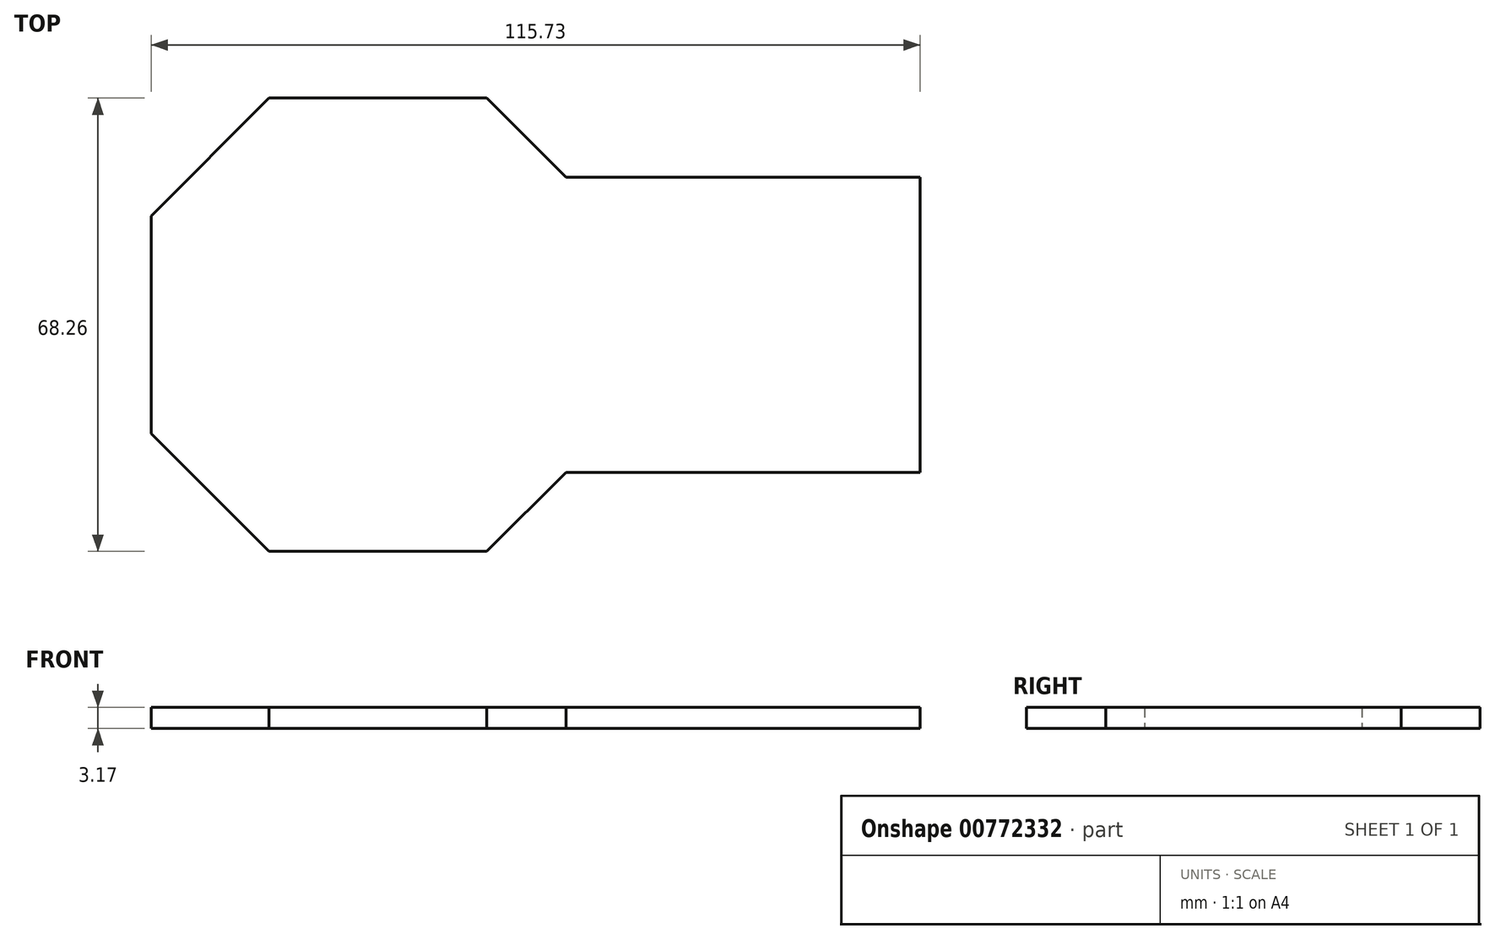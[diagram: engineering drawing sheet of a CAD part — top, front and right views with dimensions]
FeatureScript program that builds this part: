
annotation { "Feature Type Name" : "Feature", "Feature Type Description" : "" }
export const myFeature = defineFeature(function(context is Context, id is Id, definition is map)
    precondition{}
    {
        {
            var Q0;
            Q0=qCreatedBy(makeId("Top.planeOp"),FACE);
            var sketch = newSketch(context, id + "F0", { "sketchPlane" : qUnion([Q0])});
            skLineSegment(sketch, "E0.bottom", {"start": v(0, 0) * mm, "end": v(115.73, 0) * mm});
            skLineSegment(sketch, "E0.top", {"start": v(0, 68.26) * mm, "end": v(115.73, 68.26) * mm});
            skLineSegment(sketch, "E0.left", {"start": v(0, 0) * mm, "end": v(0, 68.26) * mm});
            skLineSegment(sketch, "E0.right", {"start": v(115.73, 0) * mm, "end": v(115.73, 68.26) * mm});
            skPoint(sketch, "E1", {"position": v(115.73, 11.9) * mm});
            skPoint(sketch, "E2", {"position": v(115.73, 56.36) * mm});
            skPoint(sketch, "E3", {"position": v(3.18, 3.18) * mm});
            skLineSegment(sketch, "E4.bottom", {"start": v(3.18, 3.18) * mm, "end": v(65.09, 3.18) * mm});
            skLineSegment(sketch, "E4.top", {"start": v(3.17, 65.09) * mm, "end": v(65.09, 65.09) * mm});
            skLineSegment(sketch, "E4.left", {"start": v(3.18, 3.18) * mm, "end": v(3.18, 65.09) * mm});
            skLineSegment(sketch, "E4.right", {"start": v(65.09, 3.18) * mm, "end": v(65.09, 65.09) * mm});
            skLineSegment(sketch, "E5", {"start": v(3.18, 65.09) * mm, "end": v(65.09, 3.18) * mm});
            skPoint(sketch, "E6", {"position": v(34.13, 34.13) * mm});
            skPoint(sketch, "E7", {"position": v(34.13, 65.09) * mm});
            skCircle(sketch, "E8", {"center": v(34.13, 34.13) * mm, "radius": 30.96 * mm});
            skLineSegment(sketch, "E9", {"start": v(65.09, 65.09) * mm, "end": v(3.17, 3.17) * mm});
            skPoint(sketch, "E10", {"position": v(8.87, 59.39) * mm});
            skPoint(sketch, "E11", {"position": v(59.39, 59.39) * mm});
            skPoint(sketch, "E12", {"position": v(8.87, 8.87) * mm});
            skPoint(sketch, "E13", {"position": v(59.39, 8.87) * mm});
            skPoint(sketch, "E14", {"position": v(12.24, 56.02) * mm});
            skPoint(sketch, "E15", {"position": v(56.02, 56.02) * mm});
            skPoint(sketch, "E16", {"position": v(56.02, 12.24) * mm});
            skPoint(sketch, "E17", {"position": v(12.24, 12.24) * mm});
            skPoint(sketch, "E18", {"position": v(0, 50.51) * mm});
            skLineSegment(sketch, "E19", {"start": v(17.75, 68.26) * mm, "end": v(0, 50.51) * mm});
            skLineSegment(sketch, "E20", {"start": v(34.13, 65.09) * mm, "end": v(34.13, 3.18) * mm});
            skLineSegment(sketch, "E21.MirrorCS", {"start": v(68.26, 17.75) * mm, "end": v(50.51, 0) * mm});
            skLineSegment(sketch, "E22.MirrorCS", {"start": v(0, 17.75) * mm, "end": v(17.75, 0) * mm});
            skLineSegment(sketch, "E23.MirrorCS", {"start": v(50.51, 68.26) * mm, "end": v(68.26, 50.51) * mm});
            skLineSegment(sketch, "E24", {"start": v(115.73, 56.36) * mm, "end": v(62.42, 56.36) * mm});
            skLineSegment(sketch, "E25", {"start": v(115.73, 11.9) * mm, "end": v(62.42, 11.9) * mm});
            skSolve(sketch);
        }
        {
            var Q0;
            {var subQ0=sQuery(id+"F0.wireOp",EDGE,"E8");var subQ6=makeQuery(id+"F0.imprint","INTERSECT",VERTEX,{"derivedFrom":[sQuery(id+"F0.wireOp",EDGE,"E4.left"),subQ0]});Q0=makeQuery(id+"F0.imprint","IMPRINT",FACE,{"disambiguationData":[TD([[makeQuery(id+"F0.imprint","IMPRINT",EDGE,{"disambiguationData":[TD([[subQ6,1.0]])],"derivedFrom":subQ0}),1.0]])]});}
            var Q1;
            {var subQ1=sQuery(id+"F0.wireOp",EDGE,"E8");var subQ3=sQuery(id+"F0.wireOp",EDGE,"E9");var subQ4=makeQuery(id+"F0.imprint","INTERSECT",VERTEX,{"disambiguationData":[OD(1.0)],"derivedFrom":[subQ1,subQ3]});Q1=makeQuery(id+"F0.imprint","IMPRINT",FACE,{"disambiguationData":[TD([[makeQuery(id+"F0.imprint","IMPRINT",EDGE,{"disambiguationData":[TD([[subQ4,-1.0]])],"derivedFrom":subQ1}),1.0]])]});}
            var Q2;
            {var subQ0=sQuery(id+"F0.wireOp",EDGE,"E8");var subQ5=sQuery(id+"F0.wireOp",EDGE,"E9");var subQ6=makeQuery(id+"F0.imprint","INTERSECT",VERTEX,{"disambiguationData":[OD(1.0)],"derivedFrom":[subQ0,subQ5]});Q2=makeQuery(id+"F0.imprint","IMPRINT",FACE,{"disambiguationData":[TD([[makeQuery(id+"F0.imprint","IMPRINT",EDGE,{"disambiguationData":[TD([[subQ6,-1.0]])],"derivedFrom":subQ5}),1.0]])]});}
            var Q3;
            {var subQ0=sQuery(id+"F0.wireOp",EDGE,"E21.MirrorCS");var subQ1=sQuery(id+"F0.wireOp",EDGE,"E0.bottom");var subQ2=makeQuery(id+"F0.imprint","INTERSECT",VERTEX,{"derivedFrom":[subQ1,subQ0]});Q3=makeQuery(id+"F0.imprint","IMPRINT",FACE,{"disambiguationData":[TD([[makeQuery(id+"F0.imprint","IMPRINT",EDGE,{"disambiguationData":[TD([[subQ2,1.0]])],"derivedFrom":subQ1}),1.0]])]});}
            var Q4;
            {var subQ0=sQuery(id+"F0.wireOp",EDGE,"E22.MirrorCS");var subQ1=sQuery(id+"F0.wireOp",EDGE,"E4.left");var subQ2=makeQuery(id+"F0.imprint","INTERSECT",VERTEX,{"derivedFrom":[subQ1,subQ0]});Q4=makeQuery(id+"F0.imprint","IMPRINT",FACE,{"disambiguationData":[TD([[makeQuery(id+"F0.imprint","IMPRINT",EDGE,{"disambiguationData":[TD([[subQ2,-1.0]])],"derivedFrom":subQ1}),-1.0]])]});}
            var Q5;
            {var subQ0=sQuery(id+"F0.wireOp",EDGE,"E19");var subQ1=sQuery(id+"F0.wireOp",EDGE,"E0.left");var subQ2=makeQuery(id+"F0.imprint","INTERSECT",VERTEX,{"derivedFrom":[subQ1,subQ0]});Q5=makeQuery(id+"F0.imprint","IMPRINT",FACE,{"disambiguationData":[TD([[makeQuery(id+"F0.imprint","IMPRINT",EDGE,{"disambiguationData":[TD([[subQ2,1.0]])],"derivedFrom":subQ1}),-1.0]])]});}
            var Q6;
            {var subQ0=sQuery(id+"F0.wireOp",EDGE,"E8");var subQ1=sQuery(id+"F0.wireOp",EDGE,"E4.left");var subQ2=makeQuery(id+"F0.imprint","INTERSECT",VERTEX,{"derivedFrom":[subQ1,subQ0]});Q6=makeQuery(id+"F0.imprint","IMPRINT",FACE,{"disambiguationData":[TD([[makeQuery(id+"F0.imprint","IMPRINT",EDGE,{"disambiguationData":[TD([[subQ2,-1.0]])],"derivedFrom":subQ1}),-1.0]])]});}
            var Q7;
            {var subQ3=sQuery(id+"F0.wireOp",EDGE,"E19");var subQ5=sQuery(id+"F0.wireOp",EDGE,"E5");var subQ6=makeQuery(id+"F0.imprint","INTERSECT",VERTEX,{"derivedFrom":[subQ5,subQ3]});Q7=makeQuery(id+"F0.imprint","IMPRINT",FACE,{"disambiguationData":[TD([[makeQuery(id+"F0.imprint","IMPRINT",EDGE,{"disambiguationData":[TD([[subQ6,-1.0]])],"derivedFrom":subQ5}),1.0]])]});}
            var Q8;
            {var subQ0=sQuery(id+"F0.wireOp",EDGE,"E19");var subQ1=sQuery(id+"F0.wireOp",EDGE,"E0.top");var subQ2=makeQuery(id+"F0.imprint","INTERSECT",VERTEX,{"derivedFrom":[subQ1,subQ0]});Q8=makeQuery(id+"F0.imprint","IMPRINT",FACE,{"disambiguationData":[TD([[makeQuery(id+"F0.imprint","IMPRINT",EDGE,{"disambiguationData":[TD([[subQ2,-1.0]])],"derivedFrom":subQ1}),-1.0]])]});}
            var Q9;
            {var subQ0=sQuery(id+"F0.wireOp",EDGE,"E8");var subQ1=sQuery(id+"F0.wireOp",EDGE,"E5");var subQ2=makeQuery(id+"F0.imprint","INTERSECT",VERTEX,{"disambiguationData":[OD(0.0)],"derivedFrom":[subQ1,subQ0]});Q9=makeQuery(id+"F0.imprint","IMPRINT",FACE,{"disambiguationData":[TD([[makeQuery(id+"F0.imprint","IMPRINT",EDGE,{"disambiguationData":[TD([[subQ2,-1.0]])],"derivedFrom":subQ1}),1.0]])]});}
            var Q10;
            {var subQ1=sQuery(id+"F0.wireOp",EDGE,"E8");var subQ3=sQuery(id+"F0.wireOp",EDGE,"E9");var subQ4=makeQuery(id+"F0.imprint","INTERSECT",VERTEX,{"disambiguationData":[OD(0.0)],"derivedFrom":[subQ1,subQ3]});Q10=makeQuery(id+"F0.imprint","IMPRINT",FACE,{"disambiguationData":[TD([[makeQuery(id+"F0.imprint","IMPRINT",EDGE,{"disambiguationData":[TD([[subQ4,-1.0]])],"derivedFrom":subQ1}),1.0]])]});}
            var Q11;
            {var subQ3=sQuery(id+"F0.wireOp",EDGE,"E23.MirrorCS");var subQ6=sQuery(id+"F0.wireOp",EDGE,"E4.right");var subQ7=makeQuery(id+"F0.imprint","INTERSECT",VERTEX,{"derivedFrom":[subQ6,subQ3]});Q11=makeQuery(id+"F0.imprint","IMPRINT",FACE,{"disambiguationData":[TD([[makeQuery(id+"F0.imprint","IMPRINT",EDGE,{"disambiguationData":[TD([[subQ7,1.0]])],"derivedFrom":subQ6}),1.0]])]});}
            var Q12;
            {var subQ0=sQuery(id+"F0.wireOp",EDGE,"E8");var subQ5=sQuery(id+"F0.wireOp",EDGE,"E9");var subQ6=makeQuery(id+"F0.imprint","INTERSECT",VERTEX,{"disambiguationData":[OD(0.0)],"derivedFrom":[subQ0,subQ5]});Q12=makeQuery(id+"F0.imprint","IMPRINT",FACE,{"disambiguationData":[TD([[makeQuery(id+"F0.imprint","IMPRINT",EDGE,{"disambiguationData":[TD([[subQ6,1.0]])],"derivedFrom":subQ5}),-1.0]])]});}
            var Q13;
            {var subQ0=sQuery(id+"F0.wireOp",EDGE,"E8");var subQ5=makeQuery(id+"F0.imprint","INTERSECT",VERTEX,{"derivedFrom":[sQuery(id+"F0.wireOp",EDGE,"E4.right"),subQ0]});Q13=makeQuery(id+"F0.imprint","IMPRINT",FACE,{"disambiguationData":[TD([[makeQuery(id+"F0.imprint","IMPRINT",EDGE,{"disambiguationData":[TD([[subQ5,-1.0]])],"derivedFrom":subQ0}),1.0]])]});}
            var Q14;
            {var subQ0=sQuery(id+"F0.wireOp",EDGE,"E8");var subQ1=sQuery(id+"F0.wireOp",EDGE,"E5");var subQ2=makeQuery(id+"F0.imprint","INTERSECT",VERTEX,{"disambiguationData":[OD(1.0)],"derivedFrom":[subQ1,subQ0]});Q14=makeQuery(id+"F0.imprint","IMPRINT",FACE,{"disambiguationData":[TD([[makeQuery(id+"F0.imprint","IMPRINT",EDGE,{"disambiguationData":[TD([[subQ2,1.0]])],"derivedFrom":subQ1}),-1.0]])]});}
            var Q15;
            {var subQ0=sQuery(id+"F0.wireOp",EDGE,"E8");var subQ5=sQuery(id+"F0.wireOp",EDGE,"E5");var subQ6=makeQuery(id+"F0.imprint","INTERSECT",VERTEX,{"disambiguationData":[OD(1.0)],"derivedFrom":[subQ5,subQ0]});Q15=makeQuery(id+"F0.imprint","IMPRINT",FACE,{"disambiguationData":[TD([[makeQuery(id+"F0.imprint","IMPRINT",EDGE,{"disambiguationData":[TD([[subQ6,-1.0]])],"derivedFrom":subQ5}),-1.0]])]});}
            var Q16;
            {var subQ1=sQuery(id+"F0.wireOp",EDGE,"E4.right");var subQ5=sQuery(id+"F0.wireOp",EDGE,"E21.MirrorCS");var subQ8=makeQuery(id+"F0.imprint","INTERSECT",VERTEX,{"derivedFrom":[subQ1,subQ5]});Q16=makeQuery(id+"F0.imprint","IMPRINT",FACE,{"disambiguationData":[TD([[makeQuery(id+"F0.imprint","IMPRINT",EDGE,{"disambiguationData":[TD([[subQ8,-1.0]])],"derivedFrom":subQ1}),1.0]])]});}
            var Q17;
            {var subQ5=sQuery(id+"F0.wireOp",EDGE,"E0.right");var subQ8=sQuery(id+"F0.wireOp",EDGE,"E24");var subQ9=makeQuery(id+"F0.imprint","INTERSECT",VERTEX,{"derivedFrom":[subQ5,subQ8]});Q17=makeQuery(id+"F0.imprint","IMPRINT",FACE,{"disambiguationData":[TD([[makeQuery(id+"F0.imprint","IMPRINT",EDGE,{"disambiguationData":[TD([[subQ9,1.0]])],"derivedFrom":subQ5}),1.0]])]});}
            var Q18;
            {var subQ0=sQuery(id+"F0.wireOp",EDGE,"E23.MirrorCS");var subQ1=sQuery(id+"F0.wireOp",EDGE,"E4.right");var subQ2=makeQuery(id+"F0.imprint","INTERSECT",VERTEX,{"derivedFrom":[subQ1,subQ0]});Q18=makeQuery(id+"F0.imprint","IMPRINT",FACE,{"disambiguationData":[TD([[makeQuery(id+"F0.imprint","IMPRINT",EDGE,{"disambiguationData":[TD([[subQ2,-1.0]])],"derivedFrom":subQ1}),1.0]])]});}
            var Q19;
            {var subQ0=sQuery(id+"F0.wireOp",EDGE,"E21.MirrorCS");var subQ1=sQuery(id+"F0.wireOp",EDGE,"E4.right");var subQ2=makeQuery(id+"F0.imprint","INTERSECT",VERTEX,{"derivedFrom":[subQ1,subQ0]});Q19=makeQuery(id+"F0.imprint","IMPRINT",FACE,{"disambiguationData":[TD([[makeQuery(id+"F0.imprint","IMPRINT",EDGE,{"disambiguationData":[TD([[subQ2,1.0]])],"derivedFrom":subQ1}),1.0]])]});}
            extrude(context, id + "F1", {"entities" : qUnion([Q0, Q1, Q2, Q3, Q4, Q5, Q6, Q7, Q8, Q9, Q10, Q11, Q12, Q13, Q14, Q15, Q16, Q17, Q18, Q19]), "depth" : 3.17 * mm, "offsetDistance" : 25.4 * mm});
        }
    });
